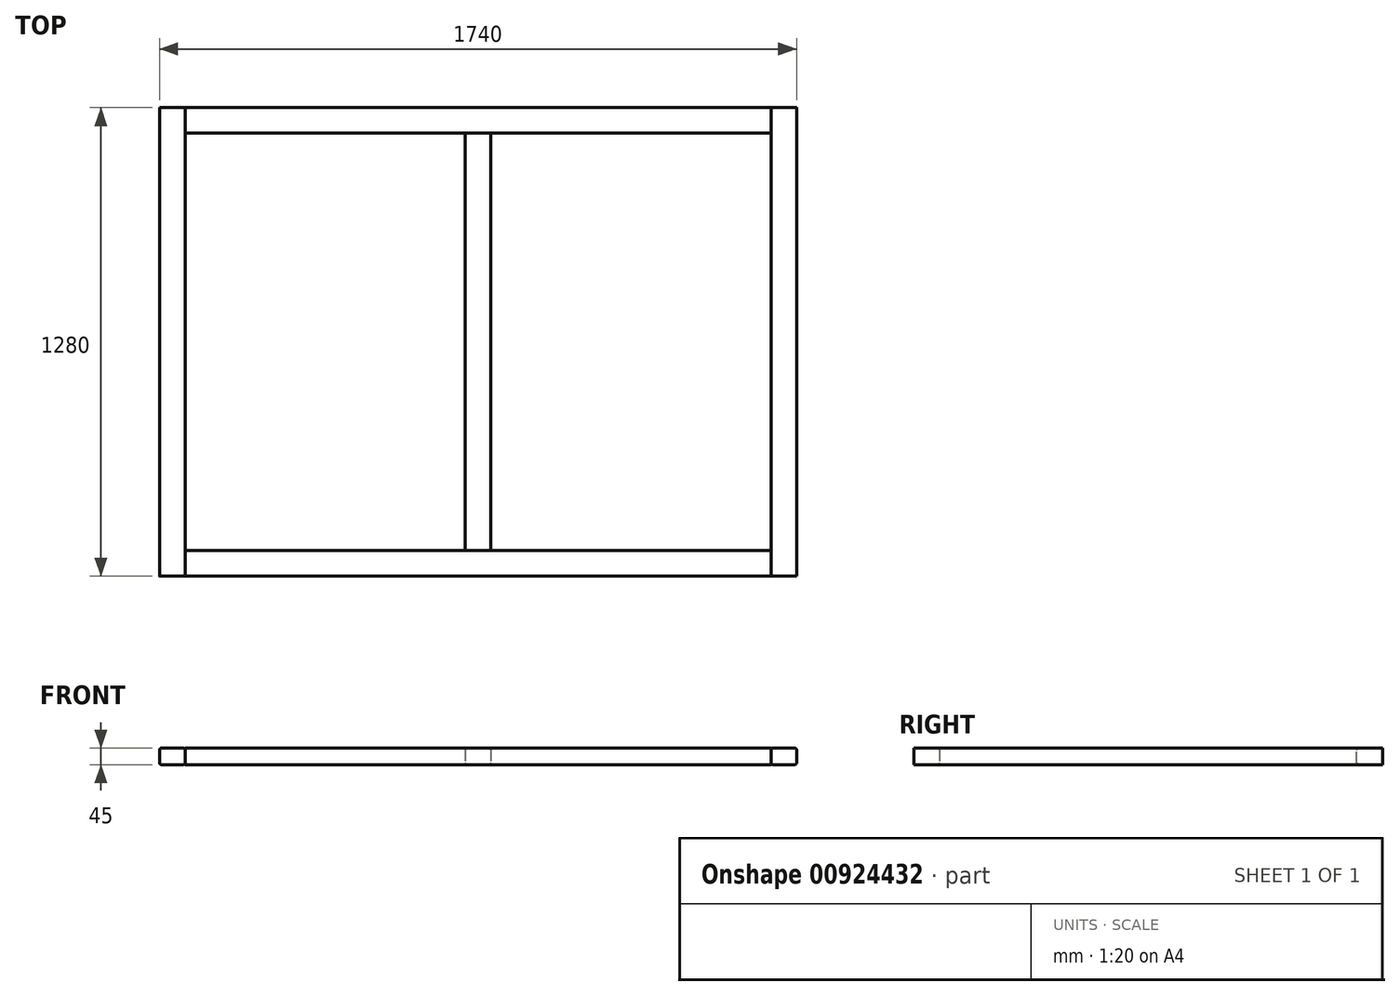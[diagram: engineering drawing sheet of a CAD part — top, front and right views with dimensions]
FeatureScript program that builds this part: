
annotation { "Feature Type Name" : "Feature", "Feature Type Description" : "" }
export const myFeature = defineFeature(function(context is Context, id is Id, definition is map)
    precondition{}
    {
        {
            var Q0;
            Q0=qCreatedBy(makeId("Front.planeOp"),FACE);
            var sketch = newSketch(context, id + "F0", { "sketchPlane" : qUnion([Q0])});
            skLineSegment(sketch, "E0.bottom", {"start": v(5, 0) * mm, "end": v(65, 0) * mm});
            skLineSegment(sketch, "E0.top", {"start": v(5, 45) * mm, "end": v(65, 45) * mm});
            skLineSegment(sketch, "E0.left", {"start": v(0, 5) * mm, "end": v(0, 40) * mm});
            skLineSegment(sketch, "E0.right", {"start": v(70, 5) * mm, "end": v(70, 40) * mm});
            skPoint(sketch, "E1.visualSharp", {"position": v(0, 45) * mm});
            skArc(sketch, "E1.filletArc", {"start": v(5, 45) * mm, "mid": v(1.46, 43.54) * mm, "end": v(0, 40) * mm});
            skPoint(sketch, "E2.visualSharp", {"position": v(70, 45) * mm});
            skArc(sketch, "E2.filletArc", {"start": v(70, 40) * mm, "mid": v(68.54, 43.54) * mm, "end": v(65, 45) * mm});
            skPoint(sketch, "E3.visualSharp", {"position": v(70, 0) * mm});
            skArc(sketch, "E3.filletArc", {"start": v(65, 0) * mm, "mid": v(68.54, 1.46) * mm, "end": v(70, 5) * mm});
            skPoint(sketch, "E4.visualSharp", {"position": v(0, 0) * mm});
            skArc(sketch, "E4.filletArc", {"start": v(0, 5) * mm, "mid": v(1.46, 1.46) * mm, "end": v(5, 0) * mm});
            skLineSegment(sketch, "E5.bottom", {"start": v(1675, 0) * mm, "end": v(1735, 0) * mm});
            skLineSegment(sketch, "E5.top", {"start": v(1675, 45) * mm, "end": v(1735, 45) * mm});
            skLineSegment(sketch, "E5.left", {"start": v(1670, 5) * mm, "end": v(1670, 40) * mm});
            skLineSegment(sketch, "E5.right", {"start": v(1740, 5) * mm, "end": v(1740, 40) * mm});
            skPoint(sketch, "E6.visualSharp", {"position": v(1670, 45) * mm});
            skArc(sketch, "E6.filletArc", {"start": v(1675, 45) * mm, "mid": v(1671.46, 43.54) * mm, "end": v(1670, 40) * mm});
            skPoint(sketch, "E7.visualSharp", {"position": v(1740, 45) * mm});
            skArc(sketch, "E7.filletArc", {"start": v(1740, 40) * mm, "mid": v(1738.54, 43.54) * mm, "end": v(1735, 45) * mm});
            skPoint(sketch, "E8.visualSharp", {"position": v(1740, 0) * mm});
            skArc(sketch, "E8.filletArc", {"start": v(1735, 0) * mm, "mid": v(1738.54, 1.46) * mm, "end": v(1740, 5) * mm});
            skPoint(sketch, "E9.visualSharp", {"position": v(1670, 0) * mm});
            skArc(sketch, "E9.filletArc", {"start": v(1670, 5) * mm, "mid": v(1671.46, 1.46) * mm, "end": v(1675, 0) * mm});
            skSolve(sketch);
        }
        {
            var Q0;
            Q0 = qSketchRegion(id + "F0", true);
            extrude(context, id + "F1", {"entities" : qUnion([Q0]), "depth" : (1300 - 20) * mm, "offsetDistance" : 25 * mm});
        }
        {
            var Q0;
            Q0=makeQuery(id+"F1.opExtrude","SWEPT_FACE",FACE,{"disambiguationData":[OSD([sQuery(id+"F0.wireOp",EDGE,"E0.right")])]});
            var sketch = newSketch(context, id + "F2", { "sketchPlane" : qUnion([Q0])});
            skLineSegment(sketch, "E10.bottom", {"start": v(-1275, 45) * mm, "end": v(-1215, 45) * mm});
            skLineSegment(sketch, "E10.top", {"start": v(-1275, 0) * mm, "end": v(-1215, 0) * mm});
            skLineSegment(sketch, "E10.left", {"start": v(-1280, 40) * mm, "end": v(-1280, 5) * mm});
            skLineSegment(sketch, "E10.right", {"start": v(-1210, 40) * mm, "end": v(-1210, 5) * mm});
            skPoint(sketch, "E11.visualSharp", {"position": v(-1280, 45) * mm});
            skArc(sketch, "E11.filletArc", {"start": v(-1275, 45) * mm, "mid": v(-1278.54, 43.54) * mm, "end": v(-1280, 40) * mm});
            skPoint(sketch, "E12.visualSharp", {"position": v(-1210, 45) * mm});
            skArc(sketch, "E12.filletArc", {"start": v(-1210, 40) * mm, "mid": v(-1211.46, 43.54) * mm, "end": v(-1215, 45) * mm});
            skPoint(sketch, "E13.visualSharp", {"position": v(-1210, 0) * mm});
            skArc(sketch, "E13.filletArc", {"start": v(-1215, 0) * mm, "mid": v(-1211.46, 1.46) * mm, "end": v(-1210, 5) * mm});
            skPoint(sketch, "E14.visualSharp", {"position": v(-1280, 0) * mm});
            skArc(sketch, "E14.filletArc", {"start": v(-1280, 5) * mm, "mid": v(-1278.54, 1.46) * mm, "end": v(-1275, 0) * mm});
            skLineSegment(sketch, "E15.bottom", {"start": v(-5, 0) * mm, "end": v(-65, 0) * mm});
            skLineSegment(sketch, "E15.top", {"start": v(-5, 45) * mm, "end": v(-65, 45) * mm});
            skLineSegment(sketch, "E15.left", {"start": v(0, 5) * mm, "end": v(0, 40) * mm});
            skLineSegment(sketch, "E15.right", {"start": v(-70, 5) * mm, "end": v(-70, 40) * mm});
            skPoint(sketch, "E16.visualSharp", {"position": v(-70, 45) * mm});
            skArc(sketch, "E16.filletArc", {"start": v(-65, 45) * mm, "mid": v(-68.54, 43.54) * mm, "end": v(-70, 40) * mm});
            skPoint(sketch, "E17.visualSharp", {"position": v(0, 45) * mm});
            skArc(sketch, "E17.filletArc", {"start": v(0, 40) * mm, "mid": v(-1.46, 43.54) * mm, "end": v(-5, 45) * mm});
            skPoint(sketch, "E18.visualSharp", {"position": v(0, 0) * mm});
            skArc(sketch, "E18.filletArc", {"start": v(-5, 0) * mm, "mid": v(-1.46, 1.46) * mm, "end": v(0, 5) * mm});
            skPoint(sketch, "E19.visualSharp", {"position": v(-70, 0) * mm});
            skArc(sketch, "E19.filletArc", {"start": v(-70, 5) * mm, "mid": v(-68.54, 1.46) * mm, "end": v(-65, 0) * mm});
            skSolve(sketch);
        }
        {
            var Q0;
            Q0 = qSketchRegion(id + "F2", true);
            var Q1;
            Q1=makeQuery(id+"F1.opExtrude","SWEPT_FACE",FACE,{"disambiguationData":[OSD([sQuery(id+"F0.wireOp",EDGE,"E5.left")])]});
            extrude(context, id + "F3", {"entities" : qUnion([Q0]), "endBound" : BoundingType.UP_TO_SURFACE, "depth" : (1600 - 140) * mm, "endBoundEntityFace" : qUnion([Q1]), "offsetDistance" : 25 * mm});
        }
        {
            var Q0;
            Q0=makeQuery(id+"F3.opExtrude","SWEPT_FACE",FACE,{"disambiguationData":[OSD([sQuery(id+"F2.wireOp",EDGE,"E15.right")])]});
            var sketch = newSketch(context, id + "F4", { "sketchPlane" : qUnion([Q0])});
            skLineSegment(sketch, "E20.bottom", {"start": v(840, 0) * mm, "end": v(900, 0) * mm});
            skLineSegment(sketch, "E20.top", {"start": v(840, 45) * mm, "end": v(900, 45) * mm});
            skLineSegment(sketch, "E20.left", {"start": v(835, 5) * mm, "end": v(835, 40) * mm});
            skLineSegment(sketch, "E20.right", {"start": v(905, 5) * mm, "end": v(905, 40) * mm});
            skPoint(sketch, "E21.visualSharp", {"position": v(835, 0) * mm});
            skArc(sketch, "E21.filletArc", {"start": v(835, 5) * mm, "mid": v(836.46, 1.46) * mm, "end": v(840, 0) * mm});
            skPoint(sketch, "E22.visualSharp", {"position": v(835, 45) * mm});
            skArc(sketch, "E22.filletArc", {"start": v(840, 45) * mm, "mid": v(836.46, 43.54) * mm, "end": v(835, 40) * mm});
            skPoint(sketch, "E23.visualSharp", {"position": v(905, 45) * mm});
            skArc(sketch, "E23.filletArc", {"start": v(905, 40) * mm, "mid": v(903.54, 43.54) * mm, "end": v(900, 45) * mm});
            skPoint(sketch, "E24.visualSharp", {"position": v(905, 0) * mm});
            skArc(sketch, "E24.filletArc", {"start": v(900, 0) * mm, "mid": v(903.54, 1.46) * mm, "end": v(905, 5) * mm});
            skSolve(sketch);
        }
        {
            var Q0;
            Q0 = qSketchRegion(id + "F4", true);
            var Q1;
            Q1=makeQuery(id+"F3.opExtrude","SWEPT_FACE",FACE,{"disambiguationData":[OSD([sQuery(id+"F2.wireOp",EDGE,"E10.right")])]});
            extrude(context, id + "F5", {"entities" : qUnion([Q0]), "endBound" : BoundingType.UP_TO_SURFACE, "depth" : 25 * mm, "endBoundEntityFace" : qUnion([Q1]), "offsetDistance" : 25 * mm});
        }
    });
